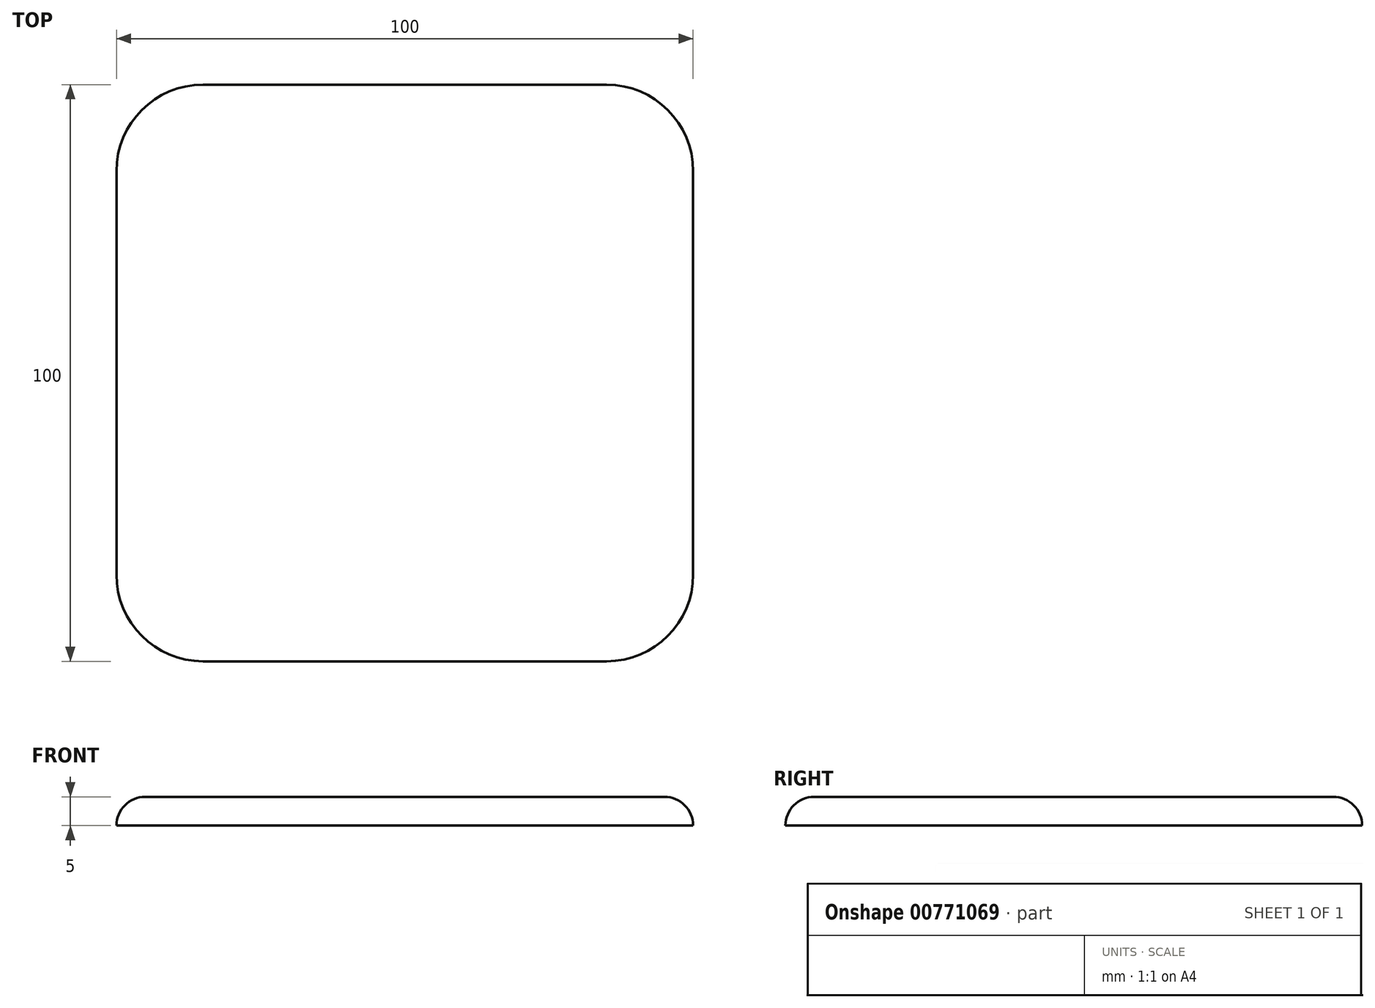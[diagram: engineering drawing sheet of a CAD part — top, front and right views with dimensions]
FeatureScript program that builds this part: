
annotation { "Feature Type Name" : "Feature", "Feature Type Description" : "" }
export const myFeature = defineFeature(function(context is Context, id is Id, definition is map)
    precondition{}
    {
        {
            var Q0;
            Q0=qCreatedBy(makeId("Top.planeOp"),FACE);
            var sketch = newSketch(context, id + "F0", { "sketchPlane" : qUnion([Q0])});
            skLineSegment(sketch, "E0.bottom", {"start": v(-35, 50) * mm, "end": v(35, 50) * mm});
            skLineSegment(sketch, "E0.top", {"start": v(-35, -50) * mm, "end": v(35, -50) * mm});
            skLineSegment(sketch, "E0.left", {"start": v(-50, 35) * mm, "end": v(-50, -35) * mm});
            skLineSegment(sketch, "E0.right", {"start": v(50, 35) * mm, "end": v(50, -35) * mm});
            skArc(sketch, "E1", {"start": v(-35, 50) * mm, "mid": v(-45.6, 45.6) * mm, "end": v(-50, 35) * mm});
            skArc(sketch, "E2", {"start": v(50, 35) * mm, "mid": v(45.6, 45.6) * mm, "end": v(35, 50) * mm});
            skArc(sketch, "E3", {"start": v(-50, -35) * mm, "mid": v(-45.6, -45.6) * mm, "end": v(-35, -50) * mm});
            skArc(sketch, "E4", {"start": v(35, -50) * mm, "mid": v(45.6, -45.6) * mm, "end": v(50, -35) * mm});
            skSolve(sketch);
        }
        {
            var Q0;
            Q0=makeQuery(id+"F0.imprint","IMPRINT",FACE,{"disambiguationData":[TD([[makeQuery(id+"F0.imprint","IMPRINT",EDGE,{"derivedFrom":sQuery(id+"F0.wireOp",EDGE,"E0.bottom")}),-1.0]])]});
            extrude(context, id + "F1", {"entities" : qUnion([Q0]), "depth" : 5 * mm, "offsetDistance" : 25 * mm});
        }
        {
            var Q0;
            Q0=makeQuery(id+"F1.opExtrude","CAP_FACE",FACE,{"disambiguationData":[OSD([sQuery(id+"F0.wireOp",EDGE,"E0.bottom"),sQuery(id+"F0.wireOp",EDGE,"E0.top"),sQuery(id+"F0.wireOp",EDGE,"E0.left"),sQuery(id+"F0.wireOp",EDGE,"E0.right"),sQuery(id+"F0.wireOp",EDGE,"E1"),sQuery(id+"F0.wireOp",EDGE,"E2"),sQuery(id+"F0.wireOp",EDGE,"E3"),sQuery(id+"F0.wireOp",EDGE,"E4")])],"isStart":false});
            fillet(context, id + "F2", {"entities" : qUnion([Q0]), "radius" : 5 * mm, "tangentPropagation" : true, "allowEdgeOverflow" : false});
        }
    });
